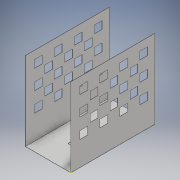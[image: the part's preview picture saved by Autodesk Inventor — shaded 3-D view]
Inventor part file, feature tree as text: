
AUTODESK INVENTOR PART (.ipt)
format: ipt  version: 2018 (Build 220112000, 112)  size: 303,616 bytes
history: native  units: in
note: dims shown in document units (in); Inventor stores cm internally (conversion verified against a paired STEP export)
features: sketch x7, extrude x6
ambient origin geometry x8: Origin, YZ Plane, XZ Plane, XY Plane, X Axis, Y Axis, Z Axis, Center Point
bodies: Solid1 (feature_tree), Solid2 (feature_tree), Solid3 (feature_tree)
feature tree (13):
  sketch  "Sketch1"  dims[d0=1.8504in d1=1.9685in]
  sketch  "Sketch2"  dims[d2=1.063in d3=1.9685in]
  extrude  "Extrusion1"  Depth=1.9685in
  extrude  "Extrusion2"  Depth=1.9685in
  sketch  "Sketch3"  dims[d4=0.0039in d5=0.0in d6=0.0039in d7=0.0in]
  extrude  "Extrusion3"  Depth=0.0039in TaperAngle=0.0deg
  extrude  "Extrusion4"  Depth=1.8504in
  extrude  "Extrusion5"  Depth=0.18in
  extrude  "Extrusion6"  Depth=0.4685in
  sketch  "Sketch4"  dims[d8=1.9685in d9=1.8504in]
  sketch  "Sketch5"  dims[d10=0.0039in d11=0.0in d12=0.18in]
  sketch  "Sketch6"  dims[d13=0.18in d14=1.1811in d16=0.4685in d17=0.3937in d19=1.0in]
  sketch  "Sketch7"  dims[d21=0.0039in d22=0.0in d23=0.18in d24=0.18in d25=1.5748in d27=0.4685in d28=1.1811in d30=0.4567in d33=0.18in d34=0.18in d35=0.7874in d37=0.4567in d38=1.1811in d40=0.4685in d43=0.0039in d44=0.0in d45=1.5748in d47=0.4685in d48=1.1811in d50=0.4567in d53=0.7874in d55=0.4567in d56=1.1811in d58=0.4685in d61=0.0039in d62=0.0in]
